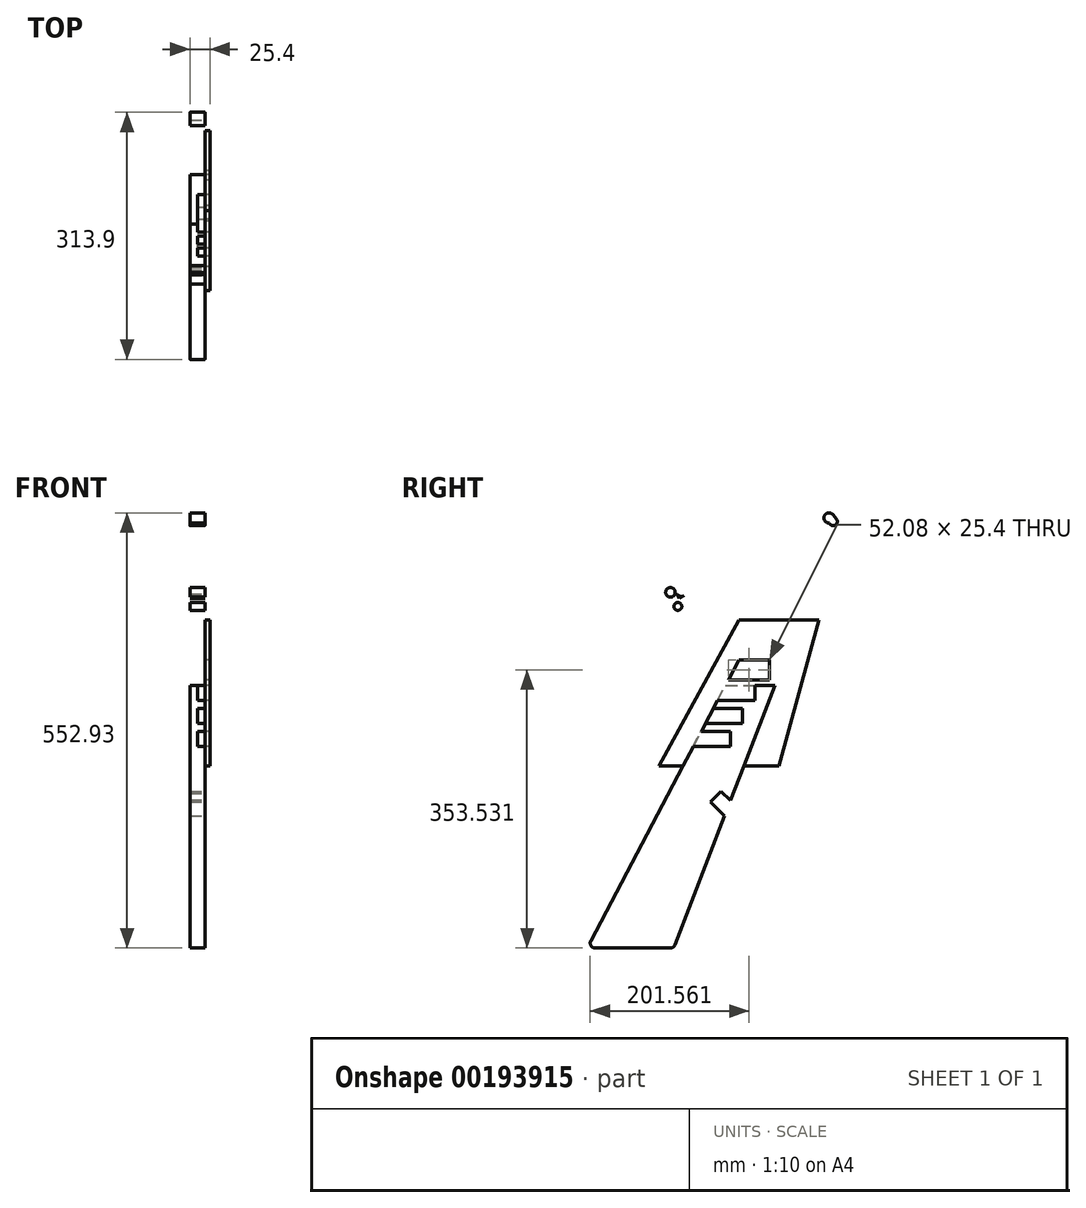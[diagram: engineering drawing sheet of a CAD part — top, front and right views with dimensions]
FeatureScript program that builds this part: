
annotation { "Feature Type Name" : "Feature", "Feature Type Description" : "" }
export const myFeature = defineFeature(function(context is Context, id is Id, definition is map)
    precondition{}
    {
        {
            var Q0;
            Q0=qCreatedBy(makeId("Right.planeOp"),FACE);
            var sketch = newSketch(context, id + "F0", { "sketchPlane" : qUnion([Q0])});
            skLineSegment(sketch, "E0", {"start": v(-99.3, 153.23) * mm, "end": v(177.61, 153.23) * mm});
            skLineSegment(sketch, "E1", {"start": v(-105.04, -176.97) * mm, "end": v(12.95, -176.97) * mm});
            skLineSegment(sketch, "E2", {"start": v(-100.07, 141.46) * mm, "end": v(177.68, 141.46) * mm});
            skLineSegment(sketch, "E3", {"start": v(173.13, 137.09) * mm, "end": v(173.13, 157.5) * mm});
            skLineSegment(sketch, "E4", {"start": v(-106.8, -179.6) * mm, "end": v(112.31, 235.92) * mm});
            skLineSegment(sketch, "E5", {"start": v(112.31, 235.92) * mm, "end": v(120.2, 250.88) * mm});
            skLineSegment(sketch, "E6", {"start": v(0.59, 252.02) * mm, "end": v(127.07, 252.02) * mm});
            skLineSegment(sketch, "E7", {"start": v(12.05, 243.94) * mm, "end": v(-11.68, 283.85) * mm});
            skLineSegment(sketch, "E8", {"start": v(11.16, 266.7) * mm, "end": v(207.45, 380.03) * mm});
            skLineSegment(sketch, "E9", {"start": v(202.62, 379.26) * mm, "end": v(216.26, 362.18) * mm});
            skLineSegment(sketch, "E10", {"start": v(214.08, 367.5) * mm, "end": v(3.16, -181.84) * mm});
            skCircle(sketch, "E11", {"center": v(-94.83, -170.59) * mm, "radius": 6.38 * mm});
            skCircle(sketch, "E12", {"center": v(0.4, -170.24) * mm, "radius": 6.73 * mm});
            skCircle(sketch, "E13", {"center": v(109.52, 245.21) * mm, "radius": 6.8 * mm});
            skCircle(sketch, "E14", {"center": v(10.08, 257) * mm, "radius": 4.99 * mm});
            skLineSegment(sketch, "E15", {"start": v(1.78, 284.99) * mm, "end": v(13.19, 265.8) * mm});
            skCircle(sketch, "E16", {"center": v(14.66, 276.5) * mm, "radius": 6.73 * mm});
            skCircle(sketch, "E17", {"center": v(202.14, 369.5) * mm, "radius": 6.47 * mm});
            skCircle(sketch, "E18", {"center": v(207.47, 364.83) * mm, "radius": 5.22 * mm});
            skCircle(sketch, "E19", {"center": v(0.69, 274.94) * mm, "radius": 6.08 * mm});
            skLineSegment(sketch, "E20", {"start": v(244.39, -179.28) * mm, "end": v(41.04, 24.6) * mm});
            skLineSegment(sketch, "E21", {"start": v(80.81, 1.24) * mm, "end": v(49.2, 32.5) * mm});
            skLineSegment(sketch, "E22", {"start": v(41.04, 24.6) * mm, "end": v(49.2, 32.5) * mm});
            skPoint(sketch, "E23", {"position": v(70.92, -5.36) * mm});
            skPoint(sketch, "E24", {"position": v(75.48, 6.52) * mm});
            skPoint(sketch, "E25", {"position": v(62.34, 19.5) * mm});
            skPoint(sketch, "E26", {"position": v(54.08, 11.53) * mm});
            skPoint(sketch, "E27", {"position": v(55.99, 9.62) * mm});
            skLineSegment(sketch, "E28", {"start": v(62.34, 19.5) * mm, "end": v(54.08, 11.53) * mm});
            skPoint(sketch, "E29", {"position": v(203.72, 377.88) * mm});
            skLineSegment(sketch, "E30", {"start": v(253.34, -164.79) * mm, "end": v(238.24, -179.54) * mm});
            skPoint(sketch, "E31", {"position": v(241.48, -176.37) * mm});
            skPoint(sketch, "E32", {"position": v(-101.36, -176.97) * mm});
            skLineSegment(sketch, "E33.0", {"start": v(241.7, -181.96) * mm, "end": v(35.65, 24.65) * mm});
            skLineSegment(sketch, "E33.1", {"start": v(35.65, 24.65) * mm, "end": v(49.23, 37.79) * mm});
            skLineSegment(sketch, "E33.2", {"start": v(83.48, 3.93) * mm, "end": v(49.23, 37.79) * mm});
            skLineSegment(sketch, "E34", {"start": v(54.08, 11.53) * mm, "end": v(51.4, 8.85) * mm});
            skLineSegment(sketch, "E35", {"start": v(62.34, 19.5) * mm, "end": v(65, 22.2) * mm});
            skLineSegment(sketch, "E36", {"start": v(83.48, 3.93) * mm, "end": v(265.64, -176.18) * mm});
            skLineSegment(sketch, "E37", {"start": v(253.34, -164.79) * mm, "end": v(253.72, -164.4) * mm});
            skLineSegment(sketch, "E38", {"start": v(238.77, -179.01) * mm, "end": v(238.24, -179.54) * mm});
            skLineSegment(sketch, "E39", {"start": v(12.95, -176.97) * mm, "end": v(261, -176.97) * mm});
            skCircle(sketch, "E40", {"center": v(238.82, -171.94) * mm, "radius": 5.03 * mm});
            skLineSegment(sketch, "E41", {"start": v(-96.64, 157.5) * mm, "end": v(-96.64, 137.24) * mm});
            skLineSegment(sketch, "E42.0", {"start": v(-99.3, 156.88) * mm, "end": v(177.61, 156.88) * mm});
            skLineSegment(sketch, "E43.0", {"start": v(-99.3, 137.83) * mm, "end": v(177.61, 137.83) * mm});
            skPoint(sketch, "E44", {"position": v(62.5, 141.46) * mm});
            skPoint(sketch, "E45", {"position": v(68.7, 153.23) * mm});
            skPoint(sketch, "E46", {"position": v(131.81, 153.23) * mm});
            skPoint(sketch, "E47", {"position": v(127.3, 141.46) * mm});
            skPoint(sketch, "E48", {"position": v(70.63, 156.88) * mm});
            skPoint(sketch, "E49", {"position": v(133.21, 156.88) * mm});
            skPoint(sketch, "E50", {"position": v(125.9, 137.83) * mm});
            skPoint(sketch, "E51", {"position": v(60.58, 137.83) * mm});
            skLineSegment(sketch, "E52", {"start": v(107.81, 156.88) * mm, "end": v(107.81, 137.83) * mm});
            skSolve(sketch);
        }
        {
            var Q0;
            {var subQ12=sQuery(id+"F0.wireOp",EDGE,"E1");var subQ14=sQuery(id+"F0.wireOp",EDGE,"E11");var subQ15=makeQuery(id+"F0.imprint","INTERSECT",VERTEX,{"derivedFrom":[subQ12,subQ14]});Q0=makeQuery(id+"F0.imprint","IMPRINT",FACE,{"disambiguationData":[TD([[makeQuery(id+"F0.imprint","IMPRINT",EDGE,{"disambiguationData":[TD([[subQ15,-1.0]])],"derivedFrom":subQ12}),1.0]])]});}
            var Q1;
            {var subQ0=sQuery(id+"F0.wireOp",EDGE,"E28");Q1=makeQuery(id+"F0.imprint","IMPRINT",FACE,{"disambiguationData":[TD([[makeQuery(id+"F0.imprint","IMPRINT",EDGE,{"derivedFrom":subQ0}),-1.0]])]});}
            var Q2;
            {var subQ0=sQuery(id+"F0.wireOp",EDGE,"E11");var subQ1=makeQuery(id+"F0.imprint","INTERSECT",VERTEX,{"derivedFrom":[sQuery(id+"F0.wireOp",EDGE,"E1"),subQ0]});Q2=makeQuery(id+"F0.imprint","IMPRINT",FACE,{"disambiguationData":[TD([[makeQuery(id+"F0.imprint","IMPRINT",EDGE,{"disambiguationData":[TD([[subQ1,1.0]])],"derivedFrom":subQ0}),1.0]])]});}
            var Q3;
            {var subQ0=sQuery(id+"F0.wireOp",EDGE,"E12");var subQ1=makeQuery(id+"F0.imprint","INTERSECT",VERTEX,{"derivedFrom":[sQuery(id+"F0.wireOp",EDGE,"E1"),subQ0]});Q3=makeQuery(id+"F0.imprint","IMPRINT",FACE,{"disambiguationData":[TD([[makeQuery(id+"F0.imprint","IMPRINT",EDGE,{"disambiguationData":[TD([[subQ1,-1.0]])],"derivedFrom":subQ0}),1.0]])]});}
            var Q4;
            {var subQ0=sQuery(id+"F0.wireOp",EDGE,"E4");var subQ1=sQuery(id+"F0.wireOp",EDGE,"E0");var subQ2=makeQuery(id+"F0.imprint","INTERSECT",VERTEX,{"derivedFrom":[subQ1,subQ0]});Q4=makeQuery(id+"F0.imprint","IMPRINT",FACE,{"disambiguationData":[TD([[makeQuery(id+"F0.imprint","IMPRINT",EDGE,{"disambiguationData":[TD([[subQ2,-1.0]])],"derivedFrom":subQ1}),-1.0]])]});}
            var Q5;
            {var subQ11=sQuery(id+"F0.wireOp",EDGE,"E0");var subQ17=sQuery(id+"F0.wireOp",EDGE,"E4");var subQ18=makeQuery(id+"F0.imprint","INTERSECT",VERTEX,{"derivedFrom":[subQ11,subQ17]});Q5=makeQuery(id+"F0.imprint","IMPRINT",FACE,{"disambiguationData":[TD([[makeQuery(id+"F0.imprint","IMPRINT",EDGE,{"disambiguationData":[TD([[subQ18,-1.0]])],"derivedFrom":subQ11}),1.0]])]});}
            var Q6;
            {var subQ0=sQuery(id+"F0.wireOp",EDGE,"E19");var subQ1=makeQuery(id+"F0.imprint","INTERSECT",VERTEX,{"derivedFrom":[sQuery(id+"F0.wireOp",EDGE,"E7"),subQ0]});Q6=makeQuery(id+"F0.imprint","IMPRINT",FACE,{"disambiguationData":[TD([[makeQuery(id+"F0.imprint","IMPRINT",EDGE,{"disambiguationData":[TD([[subQ1,1.0]])],"derivedFrom":subQ0}),1.0]])]});}
            var Q7;
            {var subQ0=sQuery(id+"F0.wireOp",EDGE,"E14");var subQ1=makeQuery(id+"F0.imprint","INTERSECT",VERTEX,{"derivedFrom":[sQuery(id+"F0.wireOp",EDGE,"E6"),subQ0]});Q7=makeQuery(id+"F0.imprint","IMPRINT",FACE,{"disambiguationData":[TD([[makeQuery(id+"F0.imprint","IMPRINT",EDGE,{"disambiguationData":[TD([[subQ1,1.0]])],"derivedFrom":subQ0}),1.0]])]});}
            var Q8;
            {var subQ0=sQuery(id+"F0.wireOp",EDGE,"E15");var subQ1=sQuery(id+"F0.wireOp",EDGE,"E8");var subQ2=makeQuery(id+"F0.imprint","INTERSECT",VERTEX,{"derivedFrom":[subQ1,subQ0]});Q8=makeQuery(id+"F0.imprint","IMPRINT",FACE,{"disambiguationData":[TD([[makeQuery(id+"F0.imprint","IMPRINT",EDGE,{"disambiguationData":[TD([[subQ2,-1.0]])],"derivedFrom":subQ1}),1.0]])]});}
            var Q9;
            {var subQ0=sQuery(id+"F0.wireOp",EDGE,"E17");var subQ1=makeQuery(id+"F0.imprint","INTERSECT",VERTEX,{"derivedFrom":[sQuery(id+"F0.wireOp",EDGE,"E9"),subQ0]});Q9=makeQuery(id+"F0.imprint","IMPRINT",FACE,{"disambiguationData":[TD([[makeQuery(id+"F0.imprint","IMPRINT",EDGE,{"disambiguationData":[TD([[subQ1,1.0]])],"derivedFrom":subQ0}),1.0]])]});}
            var Q10;
            {var subQ0=sQuery(id+"F0.wireOp",EDGE,"E18");var subQ1=sQuery(id+"F0.wireOp",EDGE,"E17");var subQ2=makeQuery(id+"F0.imprint","INTERSECT",VERTEX,{"disambiguationData":[OD(0.0)],"derivedFrom":[subQ1,subQ0]});Q10=makeQuery(id+"F0.imprint","IMPRINT",FACE,{"disambiguationData":[TD([[makeQuery(id+"F0.imprint","IMPRINT",EDGE,{"disambiguationData":[TD([[subQ2,1.0]])],"derivedFrom":subQ1}),-1.0]])]});}
            var Q11;
            {var subQ0=sQuery(id+"F0.wireOp",EDGE,"E18");var subQ1=sQuery(id+"F0.wireOp",EDGE,"E17");var subQ2=makeQuery(id+"F0.imprint","INTERSECT",VERTEX,{"disambiguationData":[OD(0.0)],"derivedFrom":[subQ1,subQ0]});Q11=makeQuery(id+"F0.imprint","IMPRINT",FACE,{"disambiguationData":[TD([[makeQuery(id+"F0.imprint","IMPRINT",EDGE,{"disambiguationData":[TD([[subQ2,1.0]])],"derivedFrom":subQ1}),1.0]])]});}
            var Q12;
            {var subQ0=sQuery(id+"F0.wireOp",EDGE,"E17");var subQ1=sQuery(id+"F0.wireOp",EDGE,"E9");var subQ2=makeQuery(id+"F0.imprint","INTERSECT",VERTEX,{"derivedFrom":[subQ1,subQ0]});Q12=makeQuery(id+"F0.imprint","IMPRINT",FACE,{"disambiguationData":[TD([[makeQuery(id+"F0.imprint","IMPRINT",EDGE,{"disambiguationData":[TD([[subQ2,-1.0]])],"derivedFrom":subQ1}),-1.0]])]});}
            var Q13;
            {var subQ3=sQuery(id+"F0.wireOp",EDGE,"E22");Q13=makeQuery(id+"F0.imprint","IMPRINT",FACE,{"disambiguationData":[TD([[makeQuery(id+"F0.imprint","IMPRINT",EDGE,{"derivedFrom":subQ3}),1.0]])]});}
            var Q14;
            {var subQ15=sQuery(id+"F0.wireOp",EDGE,"E5");var subQ16=sQuery(id+"F0.wireOp",EDGE,"E4");var subQ17=makeQuery(id+"F0.imprint","INTERSECT",VERTEX,{"derivedFrom":[subQ16,subQ15]});Q14=makeQuery(id+"F0.imprint","IMPRINT",FACE,{"disambiguationData":[TD([[makeQuery(id+"F0.imprint","IMPRINT",EDGE,{"disambiguationData":[TD([[subQ17,1.0]])],"derivedFrom":subQ16}),-1.0]])]});}
            var Q15;
            {var subQ0=sQuery(id+"F0.wireOp",EDGE,"E4");var subQ1=sQuery(id+"F0.wireOp",EDGE,"E2");var subQ2=makeQuery(id+"F0.imprint","INTERSECT",VERTEX,{"derivedFrom":[subQ1,subQ0]});Q15=makeQuery(id+"F0.imprint","IMPRINT",FACE,{"disambiguationData":[TD([[makeQuery(id+"F0.imprint","IMPRINT",EDGE,{"disambiguationData":[TD([[subQ2,-1.0]])],"derivedFrom":subQ1}),-1.0]])]});}
            var Q16;
            {var subQ0=sQuery(id+"F0.wireOp",EDGE,"E52");var subQ1=sQuery(id+"F0.wireOp",EDGE,"E0");var subQ2=makeQuery(id+"F0.imprint","INTERSECT",VERTEX,{"derivedFrom":[subQ1,subQ0]});Q16=makeQuery(id+"F0.imprint","IMPRINT",FACE,{"disambiguationData":[TD([[makeQuery(id+"F0.imprint","IMPRINT",EDGE,{"disambiguationData":[TD([[subQ2,-1.0]])],"derivedFrom":subQ1}),-1.0]])]});}
            var Q17;
            {var subQ0=sQuery(id+"F0.wireOp",EDGE,"E52");var subQ1=sQuery(id+"F0.wireOp",EDGE,"E0");var subQ2=makeQuery(id+"F0.imprint","INTERSECT",VERTEX,{"derivedFrom":[subQ1,subQ0]});Q17=makeQuery(id+"F0.imprint","IMPRINT",FACE,{"disambiguationData":[TD([[makeQuery(id+"F0.imprint","IMPRINT",EDGE,{"disambiguationData":[TD([[subQ2,-1.0]])],"derivedFrom":subQ1}),1.0]])]});}
            var Q18;
            {var subQ0=sQuery(id+"F0.wireOp",EDGE,"E52");var subQ1=sQuery(id+"F0.wireOp",EDGE,"E2");var subQ2=makeQuery(id+"F0.imprint","INTERSECT",VERTEX,{"derivedFrom":[subQ1,subQ0]});Q18=makeQuery(id+"F0.imprint","IMPRINT",FACE,{"disambiguationData":[TD([[makeQuery(id+"F0.imprint","IMPRINT",EDGE,{"disambiguationData":[TD([[subQ2,-1.0]])],"derivedFrom":subQ1}),-1.0]])]});}
            extrude(context, id + "F1", {"entities" : qUnion([Q0, Q1, Q2, Q3, Q4, Q5, Q6, Q7, Q8, Q9, Q10, Q11, Q12, Q13, Q14, Q15, Q16, Q17, Q18]), "oppositeDirection" : true, "depth" : 19.05 * mm});
        }
        {
            var Q0;
            {var subQ0=sQuery(id+"F0.wireOp",EDGE,"E4");var subQ1=sQuery(id+"F0.wireOp",EDGE,"E0");var subQ2=makeQuery(id+"F0.imprint","INTERSECT",VERTEX,{"derivedFrom":[subQ1,subQ0]});Q0=makeQuery(id+"F0.imprint","IMPRINT",FACE,{"disambiguationData":[TD([[makeQuery(id+"F0.imprint","IMPRINT",EDGE,{"disambiguationData":[TD([[subQ2,-1.0]])],"derivedFrom":subQ1}),1.0]])]});}
            var Q1;
            {var subQ0=sQuery(id+"F0.wireOp",EDGE,"E4");var subQ1=sQuery(id+"F0.wireOp",EDGE,"E0");var subQ2=makeQuery(id+"F0.imprint","INTERSECT",VERTEX,{"derivedFrom":[subQ1,subQ0]});Q1=makeQuery(id+"F0.imprint","IMPRINT",FACE,{"disambiguationData":[TD([[makeQuery(id+"F0.imprint","IMPRINT",EDGE,{"disambiguationData":[TD([[subQ2,-1.0]])],"derivedFrom":subQ1}),-1.0]])]});}
            var Q2;
            {var subQ0=sQuery(id+"F0.wireOp",EDGE,"E4");var subQ1=sQuery(id+"F0.wireOp",EDGE,"E2");var subQ2=makeQuery(id+"F0.imprint","INTERSECT",VERTEX,{"derivedFrom":[subQ1,subQ0]});Q2=makeQuery(id+"F0.imprint","IMPRINT",FACE,{"disambiguationData":[TD([[makeQuery(id+"F0.imprint","IMPRINT",EDGE,{"disambiguationData":[TD([[subQ2,-1.0]])],"derivedFrom":subQ1}),-1.0]])]});}
            extrude(context, id + "F2", {"entities" : qUnion([Q0, Q1, Q2]), "operationType" : NewBodyOperationType.REMOVE, "oppositeDirection" : true, "depth" : 9.52 * mm});
        }
        {
            var Q0;
            Q0=makeQuery(id+"F1.opExtrude","CAP_FACE",FACE,{"disambiguationData":[OSD([sQuery(id+"F0.wireOp",EDGE,"E1"),sQuery(id+"F0.wireOp",EDGE,"E4"),sQuery(id+"F0.wireOp",EDGE,"E5"),sQuery(id+"F0.wireOp",EDGE,"E6"),sQuery(id+"F0.wireOp",EDGE,"E7"),sQuery(id+"F0.wireOp",EDGE,"E8"),sQuery(id+"F0.wireOp",EDGE,"E9"),sQuery(id+"F0.wireOp",EDGE,"E10"),sQuery(id+"F0.wireOp",EDGE,"E11"),sQuery(id+"F0.wireOp",EDGE,"E12"),sQuery(id+"F0.wireOp",EDGE,"E13"),sQuery(id+"F0.wireOp",EDGE,"E14"),sQuery(id+"F0.wireOp",EDGE,"E15"),sQuery(id+"F0.wireOp",EDGE,"E16"),sQuery(id+"F0.wireOp",EDGE,"E17"),sQuery(id+"F0.wireOp",EDGE,"E18"),sQuery(id+"F0.wireOp",EDGE,"E19"),sQuery(id+"F0.wireOp",EDGE,"E28"),sQuery(id+"F0.wireOp",EDGE,"E33.0"),sQuery(id+"F0.wireOp",EDGE,"E33.2"),sQuery(id+"F0.wireOp",EDGE,"E34"),sQuery(id+"F0.wireOp",EDGE,"E35")])],"isStart":true});
            var sketch = newSketch(context, id + "F3", { "sketchPlane" : qUnion([Q0])});
            skLineSegment(sketch, "E53", {"start": v(75.99, 167.04) * mm, "end": v(123.21, 167.04) * mm});
            skLineSegment(sketch, "E54", {"start": v(123.21, 167.04) * mm, "end": v(123.21, 186.09) * mm});
            skLineSegment(sketch, "E55", {"start": v(123.21, 186.09) * mm, "end": v(86.03, 186.09) * mm});
            skLineSegment(sketch, "E56", {"start": v(55.23, 127.67) * mm, "end": v(92.4, 127.67) * mm});
            skLineSegment(sketch, "E57", {"start": v(92.4, 127.67) * mm, "end": v(92.4, 108.62) * mm});
            skLineSegment(sketch, "E58", {"start": v(92.4, 108.62) * mm, "end": v(45.18, 108.62) * mm});
            skLineSegment(sketch, "E59", {"start": v(39.82, 98.46) * mm, "end": v(77, 98.46) * mm});
            skLineSegment(sketch, "E60", {"start": v(77, 98.46) * mm, "end": v(77, 79.4) * mm});
            skLineSegment(sketch, "E61", {"start": v(77, 79.4) * mm, "end": v(29.78, 79.4) * mm});
            skSolve(sketch);
        }
        {
            var Q0;
            {var subQ0=sQuery(id+"F3.wireOp",EDGE,"E53");Q0=makeQuery(id+"F3.imprint","IMPRINT",FACE,{"disambiguationData":[TD([[makeQuery(id+"F3.imprint","IMPRINT",EDGE,{"derivedFrom":subQ0}),1.0]])]});}
            var Q1;
            {var subQ0=sQuery(id+"F3.wireOp",EDGE,"E56");Q1=makeQuery(id+"F3.imprint","IMPRINT",FACE,{"disambiguationData":[TD([[makeQuery(id+"F3.imprint","IMPRINT",EDGE,{"derivedFrom":subQ0}),-1.0]])]});}
            var Q2;
            {var subQ0=sQuery(id+"F3.wireOp",EDGE,"E59");Q2=makeQuery(id+"F3.imprint","IMPRINT",FACE,{"disambiguationData":[TD([[makeQuery(id+"F3.imprint","IMPRINT",EDGE,{"derivedFrom":subQ0}),-1.0]])]});}
            extrude(context, id + "F4", {"entities" : qUnion([Q0, Q1, Q2]), "operationType" : NewBodyOperationType.REMOVE, "oppositeDirection" : true, "depth" : 9.52 * mm});
        }
        {
            var Q0;
            Q0=makeQuery(id+"F1.opExtrude","CAP_FACE",FACE,{"disambiguationData":[OSD([sQuery(id+"F0.wireOp",EDGE,"E1"),sQuery(id+"F0.wireOp",EDGE,"E4"),sQuery(id+"F0.wireOp",EDGE,"E5"),sQuery(id+"F0.wireOp",EDGE,"E6"),sQuery(id+"F0.wireOp",EDGE,"E7"),sQuery(id+"F0.wireOp",EDGE,"E8"),sQuery(id+"F0.wireOp",EDGE,"E9"),sQuery(id+"F0.wireOp",EDGE,"E10"),sQuery(id+"F0.wireOp",EDGE,"E11"),sQuery(id+"F0.wireOp",EDGE,"E12"),sQuery(id+"F0.wireOp",EDGE,"E13"),sQuery(id+"F0.wireOp",EDGE,"E14"),sQuery(id+"F0.wireOp",EDGE,"E15"),sQuery(id+"F0.wireOp",EDGE,"E16"),sQuery(id+"F0.wireOp",EDGE,"E17"),sQuery(id+"F0.wireOp",EDGE,"E18"),sQuery(id+"F0.wireOp",EDGE,"E19"),sQuery(id+"F0.wireOp",EDGE,"E28"),sQuery(id+"F0.wireOp",EDGE,"E33.0"),sQuery(id+"F0.wireOp",EDGE,"E33.2"),sQuery(id+"F0.wireOp",EDGE,"E34"),sQuery(id+"F0.wireOp",EDGE,"E35")])],"isStart":true});
            var sketch = newSketch(context, id + "F5", { "sketchPlane" : qUnion([Q0])});
            skLineSegment(sketch, "E62.0", {"start": v(123.21, 186.09) * mm, "end": v(86.03, 186.09) * mm, "construction": true});
            skLineSegment(sketch, "E63.0", {"start": v(123.21, 167.04) * mm, "end": v(123.21, 186.09) * mm, "construction": true});
            skLineSegment(sketch, "E64.0", {"start": v(75.99, 167.04) * mm, "end": v(123.21, 167.04) * mm, "construction": true});
            skLineSegment(sketch, "E65.0", {"start": v(55.23, 127.67) * mm, "end": v(92.4, 127.67) * mm, "construction": true});
            skLineSegment(sketch, "E66.0", {"start": v(92.4, 127.67) * mm, "end": v(92.4, 108.62) * mm, "construction": true});
            skLineSegment(sketch, "E67.0", {"start": v(92.4, 108.62) * mm, "end": v(45.18, 108.62) * mm, "construction": true});
            skLineSegment(sketch, "E68.0", {"start": v(126.39, 189.26) * mm, "end": v(87.7, 189.26) * mm});
            skLineSegment(sketch, "E68.1", {"start": v(126.39, 163.86) * mm, "end": v(126.39, 189.26) * mm});
            skLineSegment(sketch, "E68.2", {"start": v(75.99, 163.86) * mm, "end": v(126.39, 163.86) * mm});
            skLineSegment(sketch, "E69", {"start": v(75.99, 163.86) * mm, "end": v(74.31, 163.86) * mm});
            skPoint(sketch, "E70", {"position": v(87.7, 189.26) * mm});
            skLineSegment(sketch, "E71.0", {"start": v(95.58, 105.44) * mm, "end": v(45.18, 105.44) * mm});
            skLineSegment(sketch, "E71.1", {"start": v(95.58, 130.84) * mm, "end": v(95.58, 105.44) * mm});
            skLineSegment(sketch, "E71.2", {"start": v(56.9, 130.84) * mm, "end": v(95.58, 130.84) * mm});
            skPoint(sketch, "E72", {"position": v(56.9, 130.84) * mm});
            skLineSegment(sketch, "E73", {"start": v(45.18, 105.44) * mm, "end": v(43.5, 105.44) * mm});
            skLineSegment(sketch, "E74.0", {"start": v(95.58, 54.64) * mm, "end": v(45.18, 54.64) * mm});
            skLineSegment(sketch, "E75.0", {"start": v(126.39, 240.06) * mm, "end": v(87.7, 240.06) * mm});
            skLineSegment(sketch, "E76", {"start": v(126.39, 240.06) * mm, "end": v(189.3, 240.06) * mm});
            skLineSegment(sketch, "E77", {"start": v(95.58, 54.64) * mm, "end": v(138.59, 54.64) * mm});
            skLineSegment(sketch, "E78", {"start": v(45.18, 54.64) * mm, "end": v(-13.81, 54.64) * mm});
            skLineSegment(sketch, "E79", {"start": v(87.7, 240.06) * mm, "end": v(-13.81, 54.64) * mm});
            skLineSegment(sketch, "E80", {"start": v(138.59, 54.64) * mm, "end": v(189.3, 240.06) * mm});
            skPoint(sketch, "E81", {"position": v(114.5, 240.06) * mm});
            skPoint(sketch, "E82", {"position": v(16.72, 54.64) * mm});
            skLineSegment(sketch, "E83", {"start": v(114.5, 240.06) * mm, "end": v(16.72, 54.64) * mm, "construction": true});
            skLineSegment(sketch, "E84", {"start": v(87.7, 189.26) * mm, "end": v(74.31, 163.86) * mm});
            skLineSegment(sketch, "E85", {"start": v(56.9, 130.84) * mm, "end": v(43.5, 105.44) * mm});
            skSolve(sketch);
        }
        {
            var Q0;
            {var subQ37=sQuery(id+"F5.wireOp",EDGE,"E68.0");Q0=makeQuery(id+"F5.imprint","IMPRINT",FACE,{"disambiguationData":[TD([[makeQuery(id+"F5.imprint","IMPRINT",EDGE,{"derivedFrom":subQ37}),-1.0]])]});}
            var Q1;
            {var subQ1=sQuery(id+"F5.wireOp",EDGE,"E77");Q1=makeQuery(id+"F5.imprint","IMPRINT",FACE,{"disambiguationData":[TD([[makeQuery(id+"F5.imprint","IMPRINT",EDGE,{"derivedFrom":subQ1}),1.0]])]});}
            extrude(context, id + "F6", {"entities" : qUnion([Q0, Q1]), "depth" : 6.35 * mm});
        }
    });
